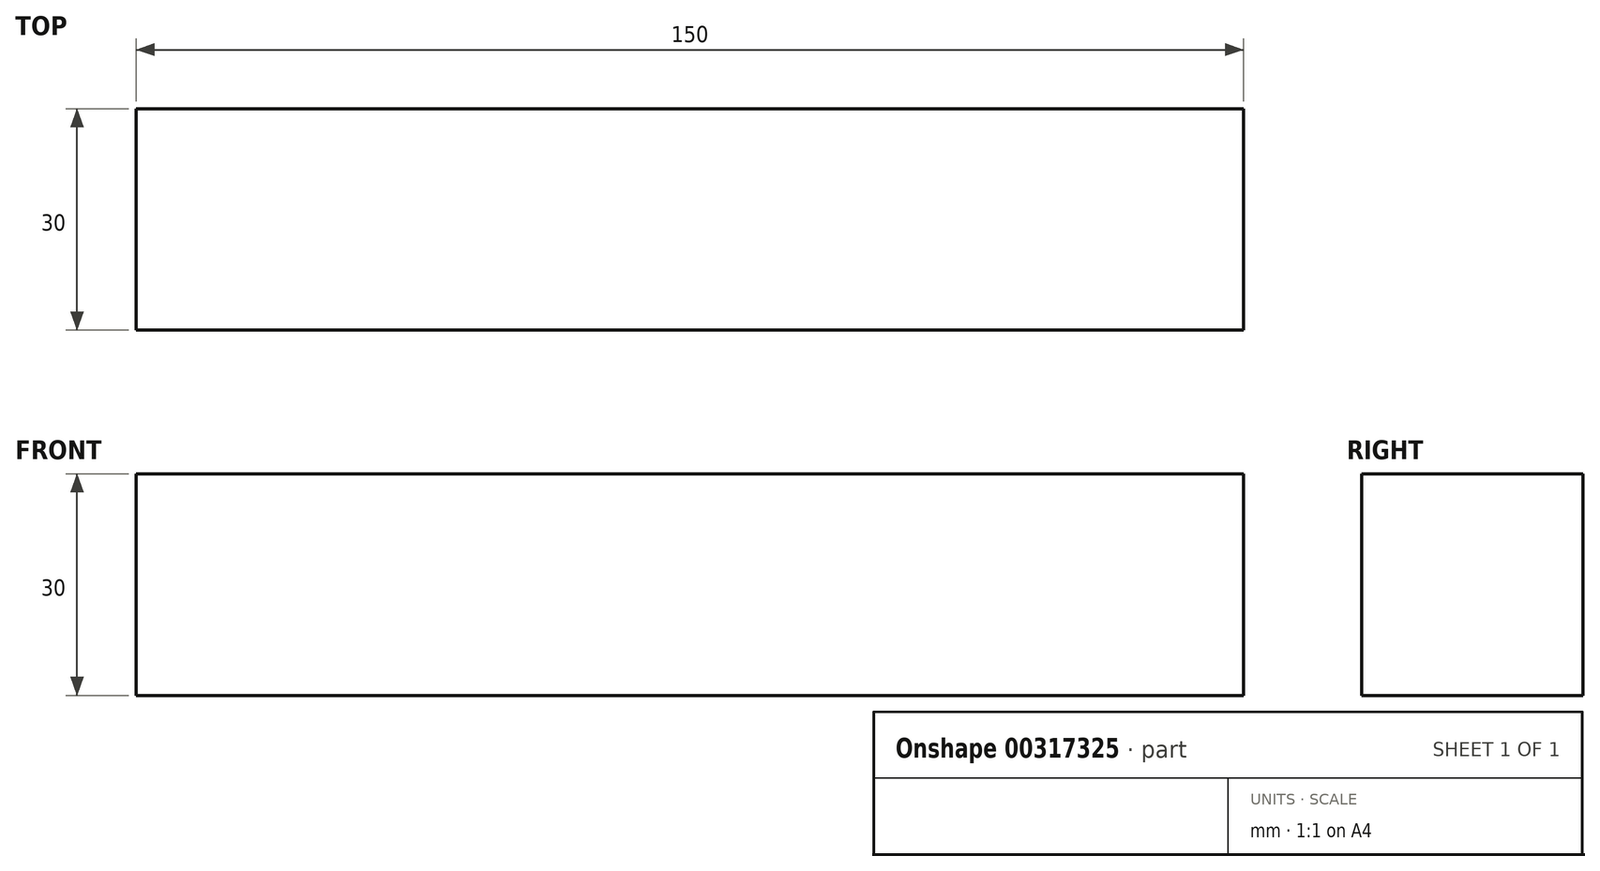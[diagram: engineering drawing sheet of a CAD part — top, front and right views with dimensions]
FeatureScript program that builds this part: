
annotation { "Feature Type Name" : "Feature", "Feature Type Description" : "" }
export const myFeature = defineFeature(function(context is Context, id is Id, definition is map)
    precondition{}
    {
        {
            var Q0;
            Q0=qCreatedBy(makeId("Right.planeOp"),FACE);
            var sketch = newSketch(context, id + "F0", { "sketchPlane" : qUnion([Q0])});
            skLineSegment(sketch, "E0.bottom", {"start": v(15, 15) * mm, "end": v(-15, 15) * mm});
            skLineSegment(sketch, "E0.top", {"start": v(15, -15) * mm, "end": v(-15, -15) * mm});
            skLineSegment(sketch, "E0.left", {"start": v(15, 15) * mm, "end": v(15, -15) * mm});
            skLineSegment(sketch, "E0.right", {"start": v(-15, 15) * mm, "end": v(-15, -15) * mm});
            skPoint(sketch, "E0.middle", {"position": v(0, 0) * mm});
            skSolve(sketch);
        }
        {
            var Q0;
            Q0 = qSketchRegion(id + "F0", true);
            extrude(context, id + "F1", {"entities" : qUnion([Q0]), "endBound" : BoundingType.SYMMETRIC, "depth" : 150 * mm});
        }
    });
